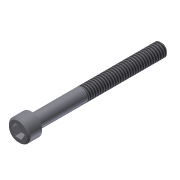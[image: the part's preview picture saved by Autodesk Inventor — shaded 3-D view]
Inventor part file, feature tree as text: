
AUTODESK INVENTOR PART (.ipt)
format: ipt  version: 2013 (Build 170138000, 138)  size: 100,352 bytes
history: native  units: in
note: dims shown in document units (in); Inventor stores cm internally (conversion verified against a paired STEP export)
features: extrude x3, sketch x3, chamfer x2, thread x1
ambient origin geometry x8: Origin, YZ Plane, XZ Plane, XY Plane, X Axis, Y Axis, Z Axis, Center Point
bodies: Solid1 (feature_tree)
feature tree (9):
  extrude  "Extrusion1"  Depth=0.164in TaperAngle=0.0deg
  extrude  "Extrusion2"  Depth=1.625in TaperAngle=0.0deg
  extrude  "Extrusion3"  Depth=0.08in TaperAngle=0.0deg
  thread  "Thread1"  [1 undecoded]
  chamfer  "Chamfer1"  Distance=0.02in Angle=45.0deg
  chamfer  "Chamfer2"  Distance=0.02in Angle=45.0deg
  sketch  "Sketch1"  dims[d0=0.27in d1=0.164in d2=0.0in]
  sketch  "Sketch2"  dims[d3=0.164in d4=1.625in d5=0.0in]
  sketch  "Sketch3"  dims[d6=0.1406in d7=0.08in d8=0.0in d9=1.0in d10=0.0in d11=0.02in d12=0.125in d13=45.0deg d14=0.02in d15=0.125in d16=45.0deg]
note: 1 required parameter value undecoded (feature->parameter linkage not recoverable at this tier; creation-order binding heuristic only, values carry confidence <= 0.55)
